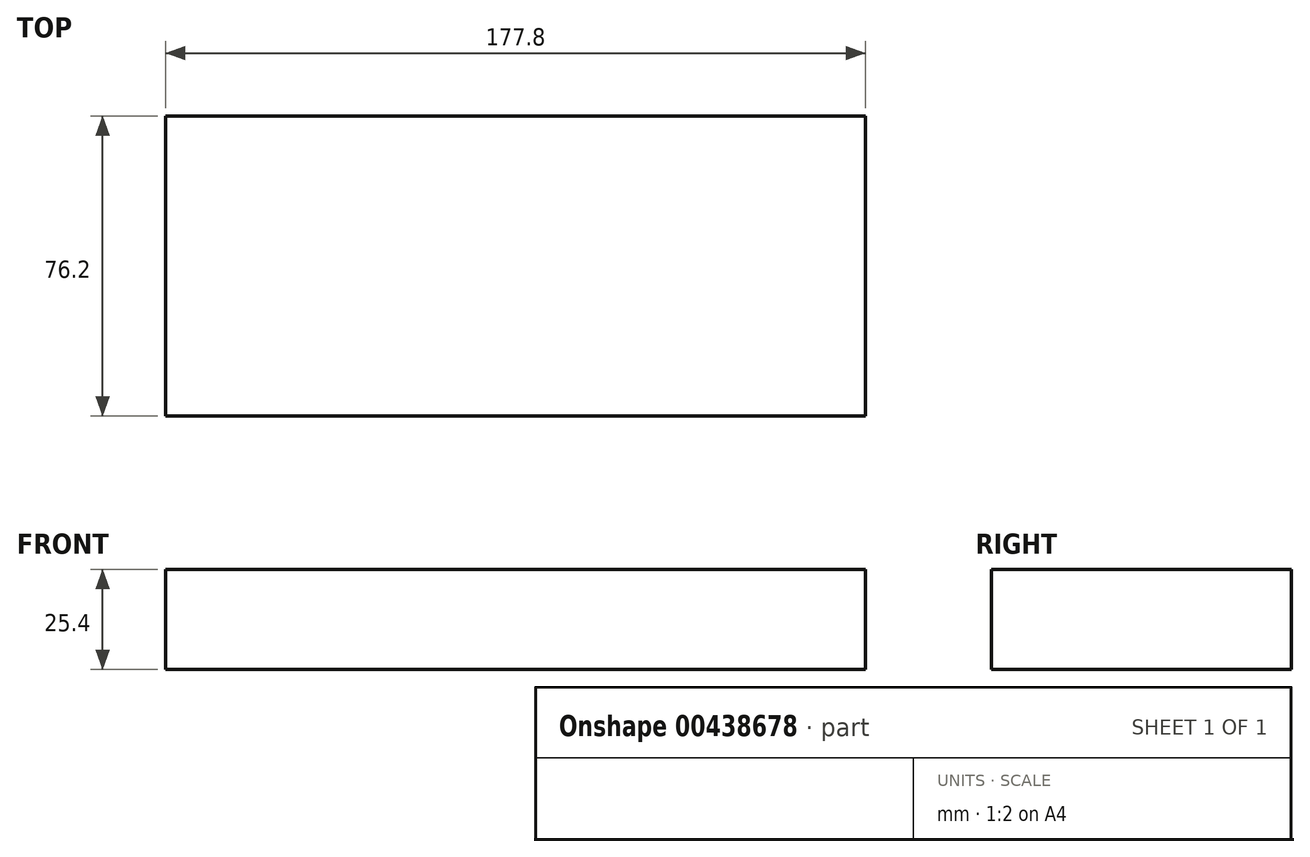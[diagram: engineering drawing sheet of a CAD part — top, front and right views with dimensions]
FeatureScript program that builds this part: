
annotation { "Feature Type Name" : "Feature", "Feature Type Description" : "" }
export const myFeature = defineFeature(function(context is Context, id is Id, definition is map)
    precondition{}
    {
        {
            var Q0;
            Q0=qCreatedBy(makeId("Top.planeOp"),FACE);
            var sketch = newSketch(context, id + "F0", { "sketchPlane" : qUnion([Q0])});
            skLineSegment(sketch, "E0.bottom", {"start": v(-98.53, -29.22) * mm, "end": v(79.27, -29.22) * mm});
            skLineSegment(sketch, "E0.top", {"start": v(-98.53, 46.98) * mm, "end": v(79.27, 46.98) * mm});
            skLineSegment(sketch, "E0.left", {"start": v(-98.53, -29.22) * mm, "end": v(-98.53, 46.98) * mm});
            skLineSegment(sketch, "E0.right", {"start": v(79.27, -29.22) * mm, "end": v(79.27, 46.98) * mm});
            skSolve(sketch);
        }
        {
            var Q0;
            Q0=makeQuery(id+"F0.imprint","IMPRINT",FACE,{"disambiguationData":[TD([[makeQuery(id+"F0.imprint","IMPRINT",EDGE,{"derivedFrom":sQuery(id+"F0.wireOp",EDGE,"E0.bottom")}),1.0]])]});
            extrude(context, id + "F1", {"entities" : qUnion([Q0]), "depth" : 25.4 * mm, "offsetDistance" : 25.4 * mm});
        }
    });
